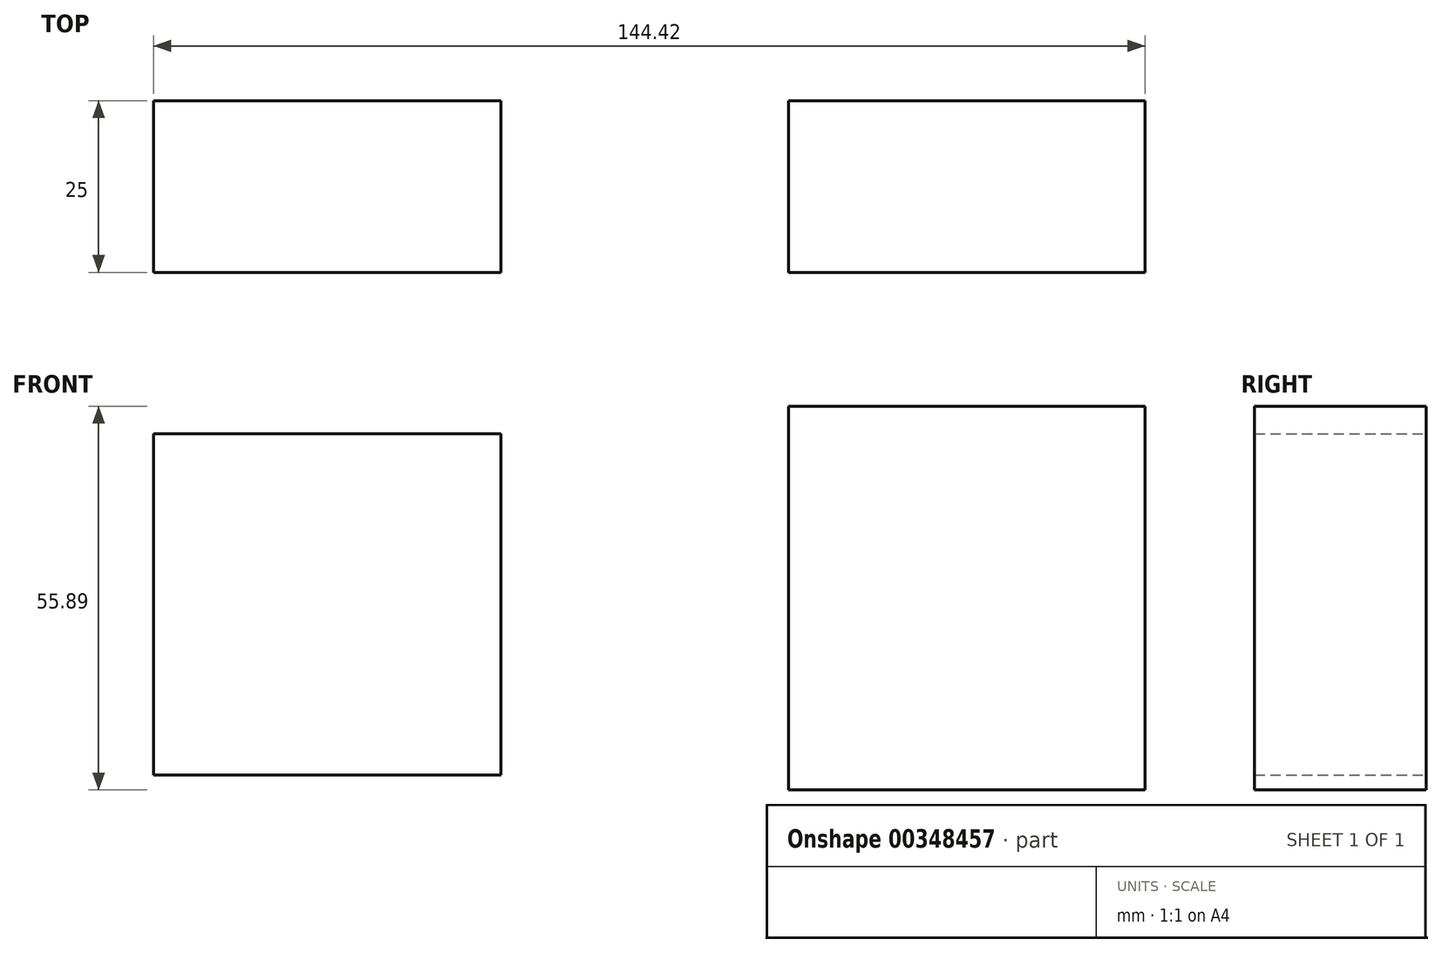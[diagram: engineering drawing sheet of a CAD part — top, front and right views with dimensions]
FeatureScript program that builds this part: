
annotation { "Feature Type Name" : "Feature", "Feature Type Description" : "" }
export const myFeature = defineFeature(function(context is Context, id is Id, definition is map)
    precondition{}
    {
        {
            var Q0;
            Q0=qCreatedBy(makeId("Front.planeOp"),FACE);
            var sketch = newSketch(context, id + "F0", { "sketchPlane" : qUnion([Q0])});
            skLineSegment(sketch, "E0.bottom", {"start": v(-102.88, 7.95) * mm, "end": v(-52.25, 7.95) * mm});
            skLineSegment(sketch, "E0.top", {"start": v(-102.88, 57.62) * mm, "end": v(-52.25, 57.62) * mm});
            skLineSegment(sketch, "E0.left", {"start": v(-102.88, 7.95) * mm, "end": v(-102.88, 57.62) * mm});
            skLineSegment(sketch, "E0.right", {"start": v(-52.25, 7.95) * mm, "end": v(-52.25, 57.62) * mm});
            skPoint(sketch, "E0.middle", {"position": v(-77.57, 32.78) * mm});
            skLineSegment(sketch, "E1.bottom", {"start": v(-10.39, 5.76) * mm, "end": v(41.54, 5.76) * mm});
            skLineSegment(sketch, "E1.top", {"start": v(-10.39, 61.65) * mm, "end": v(41.54, 61.65) * mm});
            skLineSegment(sketch, "E1.left", {"start": v(-10.39, 5.76) * mm, "end": v(-10.39, 61.65) * mm});
            skLineSegment(sketch, "E1.right", {"start": v(41.54, 5.76) * mm, "end": v(41.54, 61.65) * mm});
            skPoint(sketch, "E1.middle", {"position": v(15.58, 33.7) * mm});
            skSolve(sketch);
        }
        {
            var Q0;
            Q0=makeQuery(id+"F0.imprint","IMPRINT",FACE,{"disambiguationData":[TD([[makeQuery(id+"F0.imprint","IMPRINT",EDGE,{"derivedFrom":sQuery(id+"F0.wireOp",EDGE,"E0.bottom")}),1.0]])]});
            var Q1;
            Q1=makeQuery(id+"F0.imprint","IMPRINT",FACE,{"disambiguationData":[TD([[makeQuery(id+"F0.imprint","IMPRINT",EDGE,{"derivedFrom":sQuery(id+"F0.wireOp",EDGE,"E1.bottom")}),1.0]])]});
            extrude(context, id + "F1", {"entities" : qUnion([Q0, Q1]), "depth" : 25 * mm});
        }
    });
